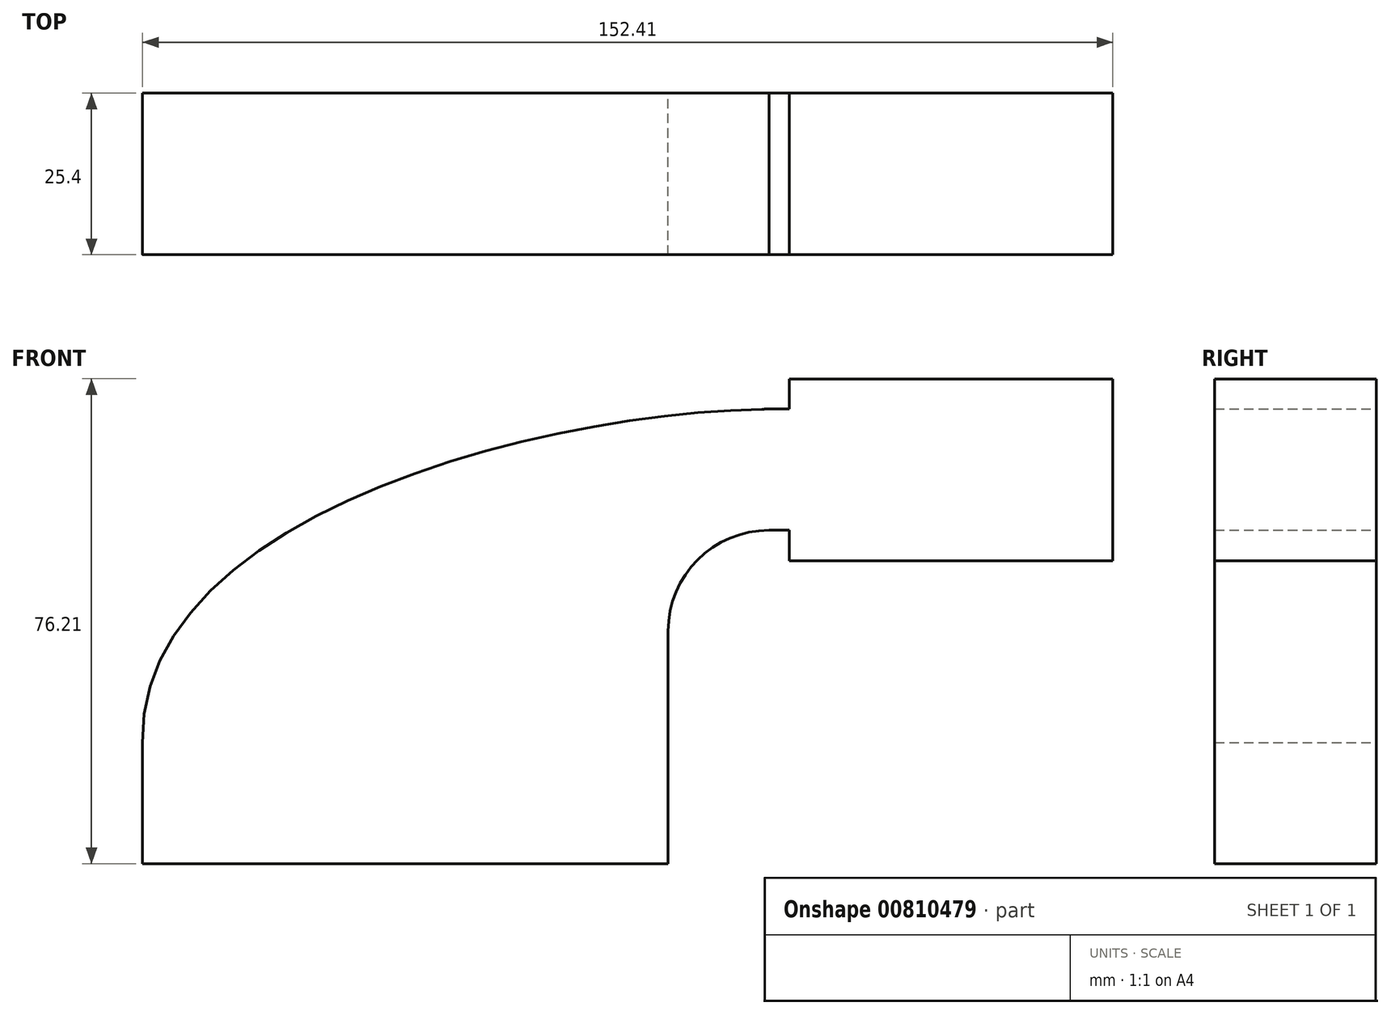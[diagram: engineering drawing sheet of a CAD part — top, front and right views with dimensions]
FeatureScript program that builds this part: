
annotation { "Feature Type Name" : "Feature", "Feature Type Description" : "" }
export const myFeature = defineFeature(function(context is Context, id is Id, definition is map)
    precondition{}
    {
        {
            var Q0;
            Q0=qCreatedBy(makeId("Front.planeOp"),FACE);
            var sketch = newSketch(context, id + "F0", { "sketchPlane" : qUnion([Q0])});
            skLineSegment(sketch, "E0.bottom", {"start": v(-41.28, -9.53) * mm, "end": v(41.28, -9.53) * mm});
            skLineSegment(sketch, "E0.top", {"start": v(-41.28, 9.53) * mm, "end": v(41.28, 9.53) * mm});
            skLineSegment(sketch, "E0.left", {"start": v(-41.28, -9.53) * mm, "end": v(-41.28, 9.53) * mm});
            skLineSegment(sketch, "E0.right", {"start": v(41.28, -9.53) * mm, "end": v(41.28, 9.53) * mm});
            skPoint(sketch, "E0.middle", {"position": v(0, 0) * mm});
            skLineSegment(sketch, "E1.bottom", {"start": v(60.32, 66.67) * mm, "end": v(111.12, 66.67) * mm});
            skLineSegment(sketch, "E1.top", {"start": v(60.33, 38.1) * mm, "end": v(111.12, 38.1) * mm});
            skLineSegment(sketch, "E1.left", {"start": v(60.32, 66.67) * mm, "end": v(60.33, 38.1) * mm});
            skLineSegment(sketch, "E1.right", {"start": v(111.12, 66.67) * mm, "end": v(111.12, 38.1) * mm});
            skPoint(sketch, "E1.middle", {"position": v(85.72, 52.39) * mm});
            skLineSegment(sketch, "E2", {"start": v(41.28, 9.53) * mm, "end": v(41.28, 27) * mm});
            skArc(sketch, "E3", {"start": v(41.27, 27) * mm, "mid": v(45.92, 38.23) * mm, "end": v(57.15, 42.88) * mm});
            skLineSegment(sketch, "E4", {"start": v(57.15, 42.88) * mm, "end": v(85.73, 42.88) * mm});
            skLineSegment(sketch, "E5.0", {"start": v(57.15, 61.93) * mm, "end": v(85.73, 61.93) * mm});
            skArc(sketch, "E5.1", {"start": v(22.23, 27) * mm, "mid": v(32.45, 51.7) * mm, "end": v(57.15, 61.93) * mm});
            skLineSegment(sketch, "E5.2", {"start": v(22.23, 9.53) * mm, "end": v(22.23, 27) * mm});
            skLineSegment(sketch, "E6", {"start": v(85.73, 38.1) * mm, "end": v(85.73, 66.68) * mm});
            skFitSpline(sketch, "E7", {"points": [v(-41.28, 9.53) * mm, v(57.15, 61.93) * mm], "startDerivative": vector(-1.94, 107.22) * mm, "endDerivative": vector(108.24, 1.34) * mm});
            skSolve(sketch);
        }
        {
            var Q0;
            Q0=makeQuery(id+"F0.imprint","IMPRINT",FACE,{"disambiguationData":[TD([[makeQuery(id+"F0.imprint","IMPRINT",EDGE,{"derivedFrom":sQuery(id+"F0.wireOp",EDGE,"E0.bottom")}),1.0]])]});
            var Q1;
            {var subQ3=sQuery(id+"F0.wireOp",EDGE,"E5.2");Q1=makeQuery(id+"F0.imprint","IMPRINT",FACE,{"disambiguationData":[TD([[makeQuery(id+"F0.imprint","IMPRINT",EDGE,{"derivedFrom":subQ3}),1.0]])]});}
            var Q2;
            {var subQ0=sQuery(id+"F0.wireOp",EDGE,"E1.left");var subQ1=sQuery(id+"F0.wireOp",EDGE,"E1.bottom");var subQ2=makeQuery(id+"F0.imprint","INTERSECT",VERTEX,{"derivedFrom":[subQ1,subQ0]});Q2=makeQuery(id+"F0.imprint","IMPRINT",FACE,{"disambiguationData":[TD([[makeQuery(id+"F0.imprint","IMPRINT",EDGE,{"disambiguationData":[TD([[subQ2,-1.0]])],"derivedFrom":subQ1}),-1.0]])]});}
            var Q3;
            {var subQ0=sQuery(id+"F0.wireOp",EDGE,"E1.left");var subQ1=sQuery(id+"F0.wireOp",EDGE,"E1.top");var subQ2=makeQuery(id+"F0.imprint","INTERSECT",VERTEX,{"derivedFrom":[subQ1,subQ0]});Q3=makeQuery(id+"F0.imprint","IMPRINT",FACE,{"disambiguationData":[TD([[makeQuery(id+"F0.imprint","IMPRINT",EDGE,{"disambiguationData":[TD([[subQ2,-1.0]])],"derivedFrom":subQ1}),1.0]])]});}
            var Q4;
            {var subQ4=sQuery(id+"F0.wireOp",EDGE,"E1.right");Q4=makeQuery(id+"F0.imprint","IMPRINT",FACE,{"disambiguationData":[TD([[makeQuery(id+"F0.imprint","IMPRINT",EDGE,{"derivedFrom":subQ4}),-1.0]])]});}
            var Q5;
            {var subQ1=sQuery(id+"F0.wireOp",EDGE,"E2");Q5=makeQuery(id+"F0.imprint","IMPRINT",FACE,{"disambiguationData":[TD([[makeQuery(id+"F0.imprint","IMPRINT",EDGE,{"derivedFrom":subQ1}),1.0]])]});}
            var Q6;
            {var subQ0=sQuery(id+"F0.wireOp",EDGE,"E5.0");var subQ1=sQuery(id+"F0.wireOp",EDGE,"E1.left");var subQ2=makeQuery(id+"F0.imprint","INTERSECT",VERTEX,{"derivedFrom":[subQ1,subQ0]});Q6=makeQuery(id+"F0.imprint","IMPRINT",FACE,{"disambiguationData":[TD([[makeQuery(id+"F0.imprint","IMPRINT",EDGE,{"disambiguationData":[TD([[subQ2,-1.0]])],"derivedFrom":subQ1}),1.0]])]});}
            extrude(context, id + "F1", {"entities" : qUnion([Q0, Q1, Q2, Q3, Q4, Q5, Q6]), "depth" : 25.4 * mm, "offsetDistance" : 25.4 * mm});
        }
    });
